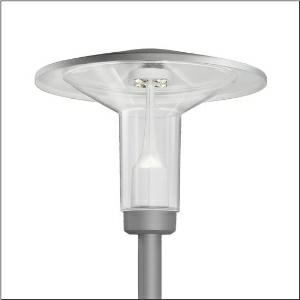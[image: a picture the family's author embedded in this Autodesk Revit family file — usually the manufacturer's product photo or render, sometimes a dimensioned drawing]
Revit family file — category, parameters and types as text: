
# Revit family: laterne_iq___pl1_2s_5xa5255rf14h_c5ef
name_source: partatom
category: Lighting Fixtures
units: mm (PartAtom-declared; Revit-internal decimal feet)

## family parameters
Cut with Voids When Loaded = No
Host = Face
Light Source = No
Part Type = Normal
Room Calculation Point = No
Round Connector Dimension = Use Diameter
Shared = No

## types (1)
- --- (1 x LED, 2970 lm, 18.5 W, 4000K)
    Apparent Load = 19 VA
    CIE Flux Codes = 25 63 94 98 100
    Color Rendering = 70
    Color Temperature = 4000K
    Default Elevation = 1800 mm
    Description = Lantern iQ, mast luminaire, Module 540 iQ-SR, primary light control with 3 zone facetted reflector, of plastic, silver coated, highly specular, structured, primary optical cover: cover, of PMMA, transparent, light distribution: PL1.2s, light emission: direct distribution, primary light characteristic: symmetric, installation type: post-top, LED, High Power LED, rated luminous flux: 2.970lm, luminous efficacy: 161lm/W, light colour: 740, colour temperature: 4000K, control gear: iQ Street-Remote, control: pre-setting: logarithmic dimming characteristic, Street-Remote, Auto-Match, Temp-Guard, Lumen-Switch, Night-Set, Smart-Wire, Light-Fading, Desk-Remote (wireless, voltage-free reading and setting of iQ features in the workshop via application-optimized NFC function/RFID function), optimised constant luminous flux control (CLO 2.0), with terminal, 6-pole, max. 2.5mm², mains connection: 230..240V, AC, 50/60Hz, start of lifetime: 19W, end of service life: 20W, reduction: 9W, luminaire housing, upper part, of glass-fibre reinforced polyester, coated, Siteco® metallic grey (DB 702S), diameter: 750mm, height: 583mm, spigot size: d x l = 76 x 70mm (post-top) | with reducer (optional accessory) 60 x 70mm, mounting height: 3..5m, post-top mast mounting element, of diecast aluminium, coated, Siteco® metallic grey (DB 702S), Module 540 iQ-SR, traffic white (RAL 9016), equipment: standard, protection rating (complete): IP65, insulation class (complete): insulation class II (safety insulation), certification: CE, ENEC, VDE, packaging unit: 1 piece

Light Distribution: PL1.2s
    Height = 583 mm
    Lamp = 1 x LED
    Lamp Light Flux = 2970 lm
    Lamp Power = 18.5 W
    Lamp count = 1
    Length = 750 mm
    Luminous efficacy = 161 lm/W
    Manufacturer = Siteco
    ModVariant = No
    Model = 5XA5255RF14H
    Number of Poles = 1
    OnlyDefault = Yes
    Power Factor = 1
    Product Name = Laterne iQ | PL1.2s
    Product group = mast luminaire | pylon top
    ProductGroupID = 6100
    Protection Class = Protection class II
    Protection Degree = IP 65
    RLX_Detail_Level = 1
    RLX_Emergency_Light_Flux = 0 lm
    RLX_Emergency_Type = 0
    RLX_Emergency_Type_DB = No
    RlxData = <blob elided: 31713 chars, md5=69ad871b>
    Socket = socket
    Standby Power = 0 W
    System Light Flux = 2970 lm
    System Power = 19 W
    Type Comments = factory setting: luminous flux: 100 % | dim-lin: 254 | 385 mA
    Type Image = l_1006050.jpg
    URL = http://relux.com
    VarID = @adj_167365
    Voltage = 0 V
    Weight = 0.00 kg
    Width = 0 mm  [stored 0 ft]

note: [stored X ft] marks values corroborated as IEEE doubles in the binary element streams (Revit-internal decimal feet)

## geometry (parser evidence)
native form markers: Blend x4, Sweep x10
no freeform markers — native parametric forms only
